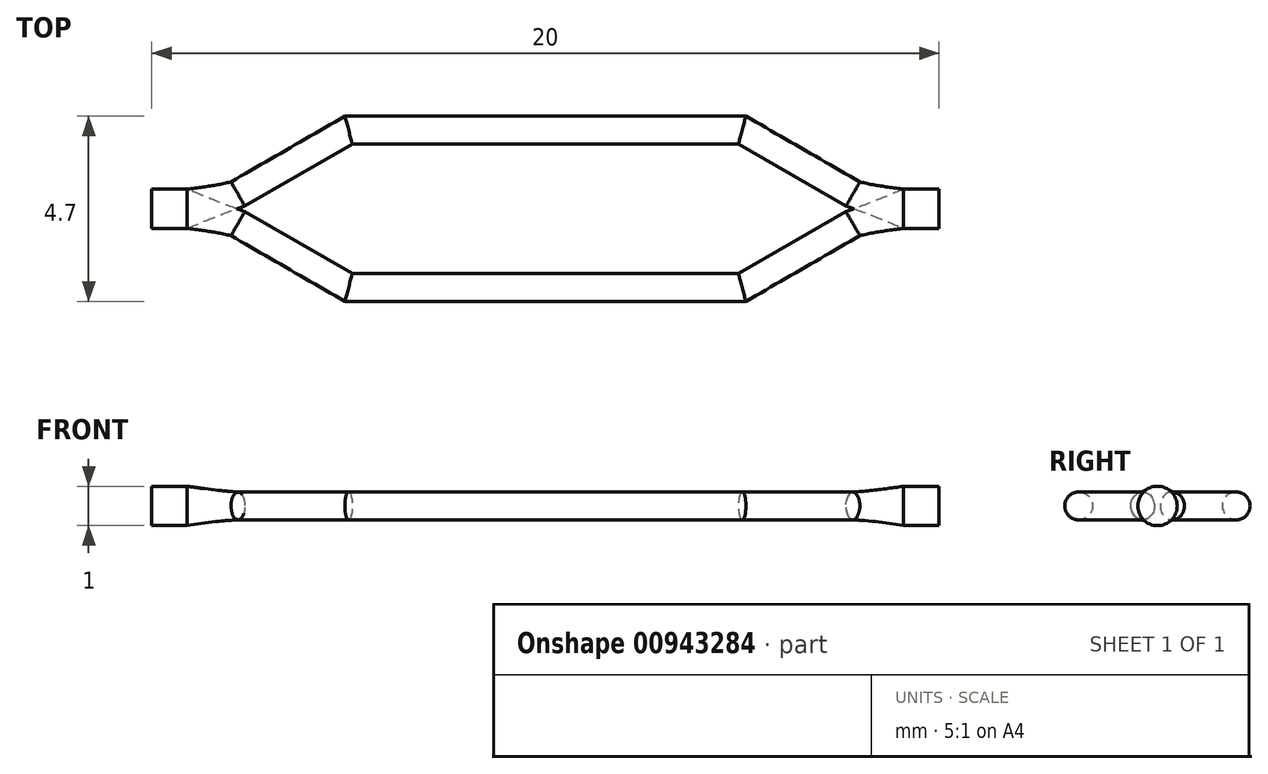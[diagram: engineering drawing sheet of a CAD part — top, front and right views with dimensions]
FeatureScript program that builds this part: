
annotation { "Feature Type Name" : "Feature", "Feature Type Description" : "" }
export const myFeature = defineFeature(function(context is Context, id is Id, definition is map)
    precondition{}
    {
        {
            var Q0;
            Q0=qCreatedBy(makeId("Top.planeOp"),FACE);
            var sketch = newSketch(context, id + "F0", { "sketchPlane" : qUnion([Q0])});
            skLineSegment(sketch, "E0.bottom", {"start": v(0, 7) * mm, "end": v(20, 7) * mm});
            skLineSegment(sketch, "E0.top", {"start": v(0, 0) * mm, "end": v(20, 0) * mm});
            skLineSegment(sketch, "E0.left", {"start": v(0, 7) * mm, "end": v(0, 0) * mm});
            skLineSegment(sketch, "E0.right", {"start": v(20, 7) * mm, "end": v(20, 0) * mm});
            skLineSegment(sketch, "E1", {"start": v(0, 3.5) * mm, "end": v(20, 3.5) * mm});
            skLineSegment(sketch, "E2", {"start": v(10, 7) * mm, "end": v(10, 0) * mm});
            skLineSegment(sketch, "E3", {"start": v(0, 3.5) * mm, "end": v(1.54, 3.5) * mm});
            skLineSegment(sketch, "E4", {"start": v(1.54, 3.5) * mm, "end": v(5, 5.5) * mm});
            skLineSegment(sketch, "E5", {"start": v(5, 5.5) * mm, "end": v(10, 5.5) * mm});
            skLineSegment(sketch, "E6", {"start": v(0, 3.5) * mm, "end": v(0.9, 3.5) * mm});
            skPoint(sketch, "E7", {"position": v(2.19, 3.88) * mm});
            skLineSegment(sketch, "E8", {"start": v(1.54, 3.5) * mm, "end": v(2.19, 3.88) * mm});
            skLineSegment(sketch, "E9", {"start": v(2.19, 3.88) * mm, "end": v(5, 5.5) * mm});
            skLineSegment(sketch, "E10", {"start": v(2.19, 3.88) * mm, "end": v(2.19, 3.5) * mm});
            skLineSegment(sketch, "E11", {"start": v(5, 5.5) * mm, "end": v(5, 3.5) * mm});
            skSolve(sketch);
        }
        {
            var Q0;
            Q0=qCreatedBy(makeId("Right.planeOp"),FACE);
            var sketch = newSketch(context, id + "F1", { "sketchPlane" : qUnion([Q0])});
            skCircle(sketch, "E12", {"center": v(3.5, 0) * mm, "radius": 0.5 * mm});
            skSolve(sketch);
        }
        {
            var Q0;
            Q0=makeQuery(id+"F1.imprint","IMPRINT",FACE,{"disambiguationData":[TD([[makeQuery(id+"F1.imprint","IMPRINT",EDGE,{"derivedFrom":sQuery(id+"F1.wireOp",EDGE,"E12")}),1.0]])]});
            var Q1;
            Q1=qSketchRegion(id+"FpUvRAgT4jxrOPf_1",true);
            var Q2;
            Q2=sQuery(id+"F0.wireOp",EDGE,"E6");
            sweep(context, id + "F2", {"profiles" : qUnion([Q0, Q1]), "path" : qUnion([Q2])});
        }
        {
            var Q0;
            Q0=sQuery(id+"F0.wireOp",EDGE,"E2");
            cPoint(context, id + "F3", {"entities" : qUnion([Q0]), "parameter" : 0.5});
        }
        {
            var Q0;
            Q0=sQuery(id+"F0.wireOp",EDGE,"E2");
            var Q1;
            Q1=qCreatedBy(id+"F3",VERTEX);
            cPlane(context, id + "F4", {"entities" : qUnion([Q0, Q1]), "cplaneType" : CPlaneType.LINE_POINT, "offset" : 25 * mm, "width" : 150 * mm, "height" : 150 * mm});
        }
        {
            var Q0;
            Q0=sQuery(id+"F0.wireOp",EDGE,"E0.bottom");
            cPoint(context, id + "F5", {"entities" : qUnion([Q0]), "parameter" : 0.5});
        }
        {
            var Q0;
            Q0=sQuery(id+"F0.wireOp",EDGE,"E0.bottom");
            var Q1;
            Q1=qCreatedBy(id+"F5",VERTEX);
            cPlane(context, id + "F6", {"entities" : qUnion([Q0, Q1]), "cplaneType" : CPlaneType.LINE_POINT, "offset" : 25 * mm, "width" : 150 * mm, "height" : 150 * mm});
        }
        {
            var Q0;
            Q0=sQuery(id+"F0.wireOp",EDGE,"E4");
            var Q1;
            Q1=sQuery(id+"F0.wireOp",VERTEX,"E7");
            var Q2;
            Q2=qBodyType(qCreatedBy(id+"F8",EDGE),BodyType.WIRE);
            cPlane(context, id + "F7", {"entities" : qUnion([Q0, Q1, Q2]), "cplaneType" : CPlaneType.LINE_POINT, "offset" : 25 * mm, "width" : 150 * mm, "height" : 150 * mm});
        }
        {
            var Q0;
            Q0=qCreatedBy(id+"F7.planeOp",FACE);
            var sketch = newSketch(context, id + "F8", { "sketchPlane" : qUnion([Q0])});
            skCircle(sketch, "E13", {"center": v(2.26, 0) * mm, "radius": 0.35 * mm});
            skSolve(sketch);
        }
        {
            var Q0;
            Q0=makeQuery(id+"F8.imprint","IMPRINT",FACE,{"disambiguationData":[TD([[makeQuery(id+"F8.imprint","IMPRINT",EDGE,{"derivedFrom":sQuery(id+"F8.wireOp",EDGE,"E13")}),1.0]])]});
            var Q1;
            Q1=sQuery(id+"F0.wireOp",EDGE,"E9");
            var Q2;
            Q2=sQuery(id+"F0.wireOp",EDGE,"E5");
            sweep(context, id + "F9", {"profiles" : qUnion([Q0]), "path" : qUnion([Q1, Q2])});
        }
        {
            var Q0;
            Q0=makeQuery(id+"F2.opSweep","CAP_FACE",FACE,{"disambiguationData":[OSD([sQuery(id+"F0.wireOp",VERTEX,"E6.end"),sQuery(id+"F1.wireOp",EDGE,"E12")])],"isStart":false});
            var Q1;
            Q1=makeQuery(id+"F9.opSweep","CAP_FACE",FACE,{"disambiguationData":[OSD([sQuery(id+"F0.wireOp",VERTEX,"E9.start"),sQuery(id+"F8.wireOp",EDGE,"E13")])],"isStart":true});
            var Q2;
            Q2=makeQuery(id+"F2.opSweep","CAP_FACE",FACE,{"disambiguationData":[OSD([sQuery(id+"F0.wireOp",VERTEX,"E6.end"),sQuery(id+"F1.wireOp",EDGE,"E12")])],"isStart":false});
            var Q3;
            Q3=makeQuery(id+"F9.opSweep","CAP_FACE",FACE,{"disambiguationData":[OSD([sQuery(id+"F0.wireOp",VERTEX,"E9.start"),sQuery(id+"F8.wireOp",EDGE,"E13")])],"isStart":true});
            var Q4;
            Q4=sQuery(id+"F0.wireOp",VERTEX,"E6.end");
            var Q5;
            Q5=sQuery(id+"F0.wireOp",VERTEX,"E7");
            loft(context, id + "F10", {"sheetProfilesArray" : [{ "sheetProfileEntities" : qUnion([Q0]) }, { "sheetProfileEntities" : qUnion([Q1]) }], "wireProfilesArray" : [{ "wireProfileEntities" : qUnion([Q2]) }, { "wireProfileEntities" : qUnion([Q3]) }], "connections" : [{ "connectionEntities" : qUnion([Q4, Q5]), "connectionEdgeQueries" : qUnion([]), "connectionEdgeParameters" : [] }]});
        }
        {
            var Q0;
            Q0=makeQuery(id+"F2.opSweep","SWEPT_BODY",BODY,{"disambiguationData":[OSD([sQuery(id+"F0.wireOp",EDGE,"E6"),sQuery(id+"F1.wireOp",EDGE,"E12")])]});
            var Q1;
            Q1=makeQuery(id+"F10.opLoft","SWEPT_BODY",BODY,{"disambiguationData":[OSD([sQuery(id+"F0.wireOp",VERTEX,"E6.end"),sQuery(id+"F0.wireOp",VERTEX,"E9.start"),sQuery(id+"F1.wireOp",EDGE,"E12"),sQuery(id+"F8.wireOp",EDGE,"E13")])]});
            var Q2;
            Q2=makeQuery(id+"F9.opSweep","SWEPT_BODY",BODY,{"disambiguationData":[OSD([sQuery(id+"F0.wireOp",EDGE,"E5"),sQuery(id+"F8.wireOp",EDGE,"E13")])]});
            var Q3;
            Q3=qCreatedBy(id+"F6.planeOp",FACE);
            mirror(context, id + "F11", {"operationType" : NewBodyOperationType.ADD, "entities" : qUnion([Q0, Q1, Q2]), "mirrorPlane" : qUnion([Q3])});
        }
        {
            var Q0;
            Q0=makeQuery(id+"F2.opSweep","SWEPT_BODY",BODY,{"disambiguationData":[OSD([sQuery(id+"F0.wireOp",EDGE,"E6"),sQuery(id+"F1.wireOp",EDGE,"E12")])]});
            var Q1;
            Q1=makeQuery(id+"F10.opLoft","SWEPT_BODY",BODY,{"disambiguationData":[OSD([sQuery(id+"F0.wireOp",VERTEX,"E6.end"),sQuery(id+"F0.wireOp",VERTEX,"E9.start"),sQuery(id+"F1.wireOp",EDGE,"E12"),sQuery(id+"F8.wireOp",EDGE,"E13")])]});
            var Q2;
            Q2=makeQuery(id+"F9.opSweep","SWEPT_BODY",BODY,{"disambiguationData":[OSD([sQuery(id+"F0.wireOp",EDGE,"E5"),sQuery(id+"F8.wireOp",EDGE,"E13")])]});
            var Q3;
            Q3=qCreatedBy(id+"F4.planeOp",FACE);
            mirror(context, id + "F12", {"entities" : qUnion([Q0, Q1, Q2]), "mirrorPlane" : qUnion([Q3])});
        }
    });
